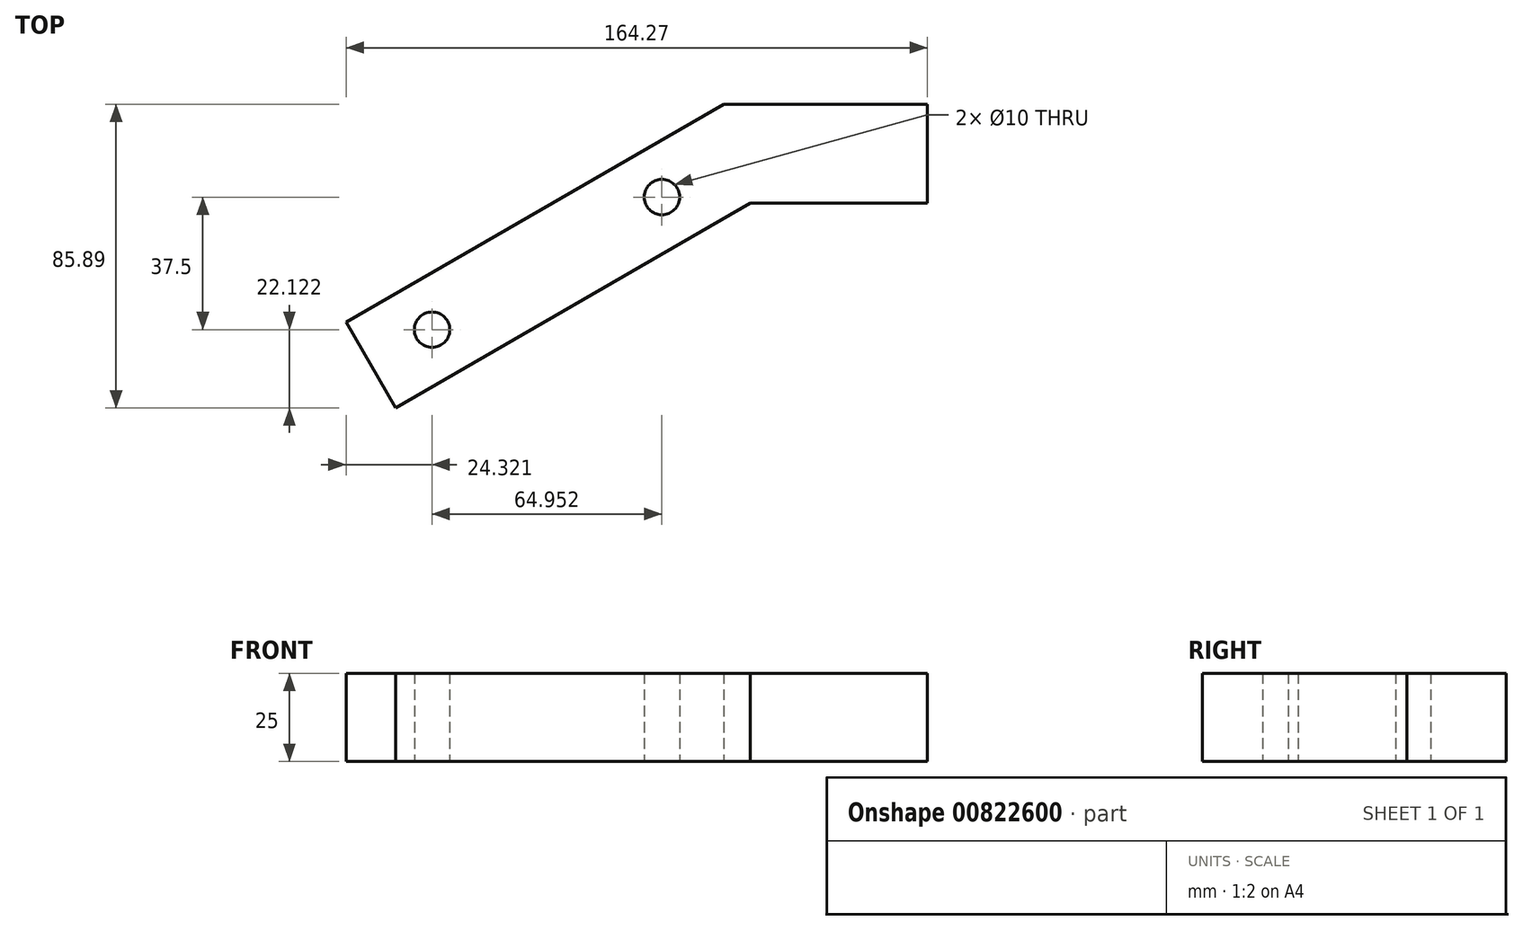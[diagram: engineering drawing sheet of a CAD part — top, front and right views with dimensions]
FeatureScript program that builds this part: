
annotation { "Feature Type Name" : "Feature", "Feature Type Description" : "" }
export const myFeature = defineFeature(function(context is Context, id is Id, definition is map)
    precondition{}
    {
        {
            var Q0;
            Q0=qCreatedBy(makeId("Top.planeOp"),FACE);
            var sketch = newSketch(context, id + "F0", { "sketchPlane" : qUnion([Q0])});
            skLineSegment(sketch, "E0", {"start": v(-106.77, -33.64) * mm, "end": v(0, 28) * mm});
            skLineSegment(sketch, "E1", {"start": v(0, 28) * mm, "end": v(57.5, 28) * mm});
            skLineSegment(sketch, "E2.0", {"start": v(7.5, 0) * mm, "end": v(57.5, 0) * mm});
            skLineSegment(sketch, "E2.1", {"start": v(-92.77, -57.9) * mm, "end": v(7.5, 0) * mm});
            skLineSegment(sketch, "E3", {"start": v(57.5, 28) * mm, "end": v(57.5, 0) * mm});
            skLineSegment(sketch, "E4", {"start": v(-106.77, -33.64) * mm, "end": v(-92.77, -57.9) * mm});
            skCircle(sketch, "E5", {"center": v(-82.45, -35.77) * mm, "radius": 5 * mm});
            skCircle(sketch, "E6", {"center": v(-17.5, 1.73) * mm, "radius": 5 * mm});
            skLineSegment(sketch, "E7", {"start": v(7.5, -20.63) * mm, "end": v(7.5, 38.03) * mm, "construction": true});
            skSolve(sketch);
        }
        {
            var Q0;
            Q0=makeQuery(id+"F0.imprint","IMPRINT",FACE,{"disambiguationData":[TD([[makeQuery(id+"F0.imprint","IMPRINT",EDGE,{"derivedFrom":sQuery(id+"F0.wireOp",EDGE,"E0")}),-1.0]])]});
            extrude(context, id + "F1", {"entities" : qUnion([Q0]), "depth" : 25 * mm, "offsetDistance" : 25 * mm});
        }
    });
